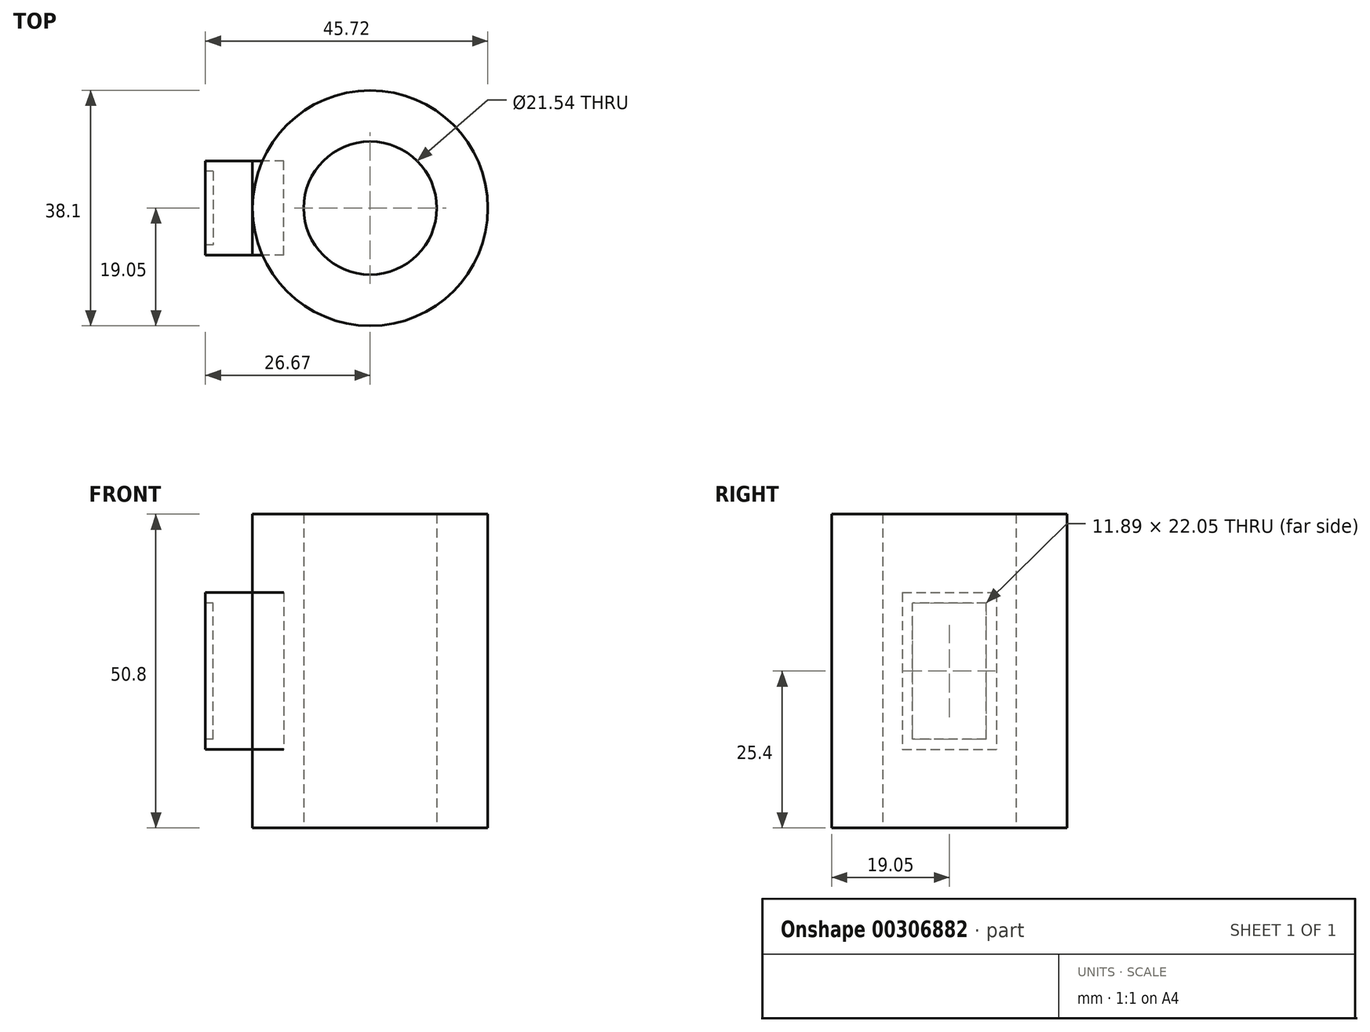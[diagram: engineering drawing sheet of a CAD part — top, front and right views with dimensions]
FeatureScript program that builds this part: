
annotation { "Feature Type Name" : "Feature", "Feature Type Description" : "" }
export const myFeature = defineFeature(function(context is Context, id is Id, definition is map)
    precondition{}
    {
        {
            var Q0;
            Q0=qCreatedBy(makeId("Top.planeOp"),FACE);
            var sketch = newSketch(context, id + "F0", { "sketchPlane" : qUnion([Q0])});
            skCircle(sketch, "E0", {"center": v(0, 0) * mm, "radius": 10.77 * mm});
            skCircle(sketch, "E1", {"center": v(0, 0) * mm, "radius": 19.05 * mm});
            skSolve(sketch);
        }
        {
            var Q0;
            Q0=makeQuery(id+"F0.imprint","IMPRINT",FACE,{"disambiguationData":[TD([[makeQuery(id+"F0.imprint","IMPRINT",EDGE,{"derivedFrom":sQuery(id+"F0.wireOp",EDGE,"E0")}),-1.0]])]});
            extrude(context, id + "F1", {"entities" : qUnion([Q0]), "depth" : 50.8 * mm});
        }
        {
            var Q0;
            Q0=qCreatedBy(makeId("Front.planeOp"),FACE);
            var sketch = newSketch(context, id + "F2", { "sketchPlane" : qUnion([Q0])});
            skLineSegment(sketch, "E2", {"start": v(-19.05, 38.1) * mm, "end": v(-26.67, 38.1) * mm});
            skLineSegment(sketch, "E3", {"start": v(-26.67, 38.1) * mm, "end": v(-26.67, 12.7) * mm});
            skLineSegment(sketch, "E4", {"start": v(-26.67, 12.7) * mm, "end": v(-19.05, 12.7) * mm});
            skLineSegment(sketch, "E5", {"start": v(-19.05, 50.8) * mm, "end": v(-19.05, 0) * mm, "construction": true});
            skLineSegment(sketch, "E6", {"start": v(0, 0) * mm, "end": v(-19.05, 0) * mm, "construction": true});
            skLineSegment(sketch, "E7", {"start": v(-26.67, 25.4) * mm, "end": v(-19.05, 25.4) * mm, "construction": true});
            skLineSegment(sketch, "E8", {"start": v(-19.05, 38.1) * mm, "end": v(-19.05, 12.7) * mm});
            skSolve(sketch);
        }
        {
            var Q0;
            Q0=makeQuery(id+"F2.imprint","IMPRINT",FACE,{"disambiguationData":[TD([[makeQuery(id+"F2.imprint","IMPRINT",EDGE,{"derivedFrom":sQuery(id+"F2.wireOp",EDGE,"E2")}),1.0]])]});
            extrude(context, id + "F3", {"entities" : qUnion([Q0]), "depth" : 7.62 * mm});
        }
        {
            var Q0;
            Q0=makeQuery(id+"F3.opExtrude","CAP_FACE",FACE,{"disambiguationData":[OSD([sQuery(id+"F2.wireOp",EDGE,"E2"),sQuery(id+"F2.wireOp",EDGE,"E3"),sQuery(id+"F2.wireOp",EDGE,"E4"),sQuery(id+"F2.wireOp",EDGE,"E8")])],"isStart":true});
            extrude(context, id + "F4", {"entities" : qUnion([Q0]), "operationType" : NewBodyOperationType.ADD, "depth" : 7.62 * mm});
        }
        {
            var Q0;
            {var subQ0=sQuery(id+"F2.wireOp",EDGE,"E3");Q0=makeQuery(id+"F4.boolean.opBoolean","MERGE",FACE,{"derivedFrom":[makeQuery(id+"F3.opExtrude","SWEPT_FACE",FACE,{"disambiguationData":[OSD([subQ0])]}),makeQuery(id+"F4.opExtrude","SWEPT_FACE",FACE,{"disambiguationData":[OSD([subQ0])]})]});}
            var sketch = newSketch(context, id + "F5", { "sketchPlane" : qUnion([Q0])});
            skLineSegment(sketch, "E9.bottom", {"start": v(-7.62, 12.7) * mm, "end": v(7.62, 12.7) * mm});
            skLineSegment(sketch, "E9.top", {"start": v(-7.62, 38.1) * mm, "end": v(7.62, 38.1) * mm});
            skLineSegment(sketch, "E9.left", {"start": v(-7.62, 12.7) * mm, "end": v(-7.62, 38.1) * mm});
            skLineSegment(sketch, "E9.right", {"start": v(7.62, 12.7) * mm, "end": v(7.62, 38.1) * mm});
            skSolve(sketch);
        }
        {
            var Q0;
            Q0=makeQuery(id+"F5.imprint","IMPRINT",FACE,{"disambiguationData":[TD([[makeQuery(id+"F5.imprint","IMPRINT",EDGE,{"derivedFrom":sQuery(id+"F5.wireOp",EDGE,"E9.bottom")}),-1.0]])]});
            extrude(context, id + "F6", {"entities" : qUnion([Q0]), "oppositeDirection" : true, "depth" : 12.7 * mm});
        }
        {
            var Q0;
            {var subQ0=sQuery(id+"F2.wireOp",EDGE,"E3");Q0=makeQuery(id+"F4.boolean.opBoolean","MERGE",FACE,{"derivedFrom":[makeQuery(id+"F3.opExtrude","SWEPT_FACE",FACE,{"disambiguationData":[OSD([subQ0])]}),makeQuery(id+"F4.opExtrude","SWEPT_FACE",FACE,{"disambiguationData":[OSD([subQ0])]})]});}
            var sketch = newSketch(context, id + "F7", { "sketchPlane" : qUnion([Q0])});
            skLineSegment(sketch, "E10.bottom", {"start": v(-5.94, 14.38) * mm, "end": v(5.94, 14.38) * mm});
            skLineSegment(sketch, "E10.top", {"start": v(-5.94, 36.42) * mm, "end": v(5.94, 36.42) * mm});
            skLineSegment(sketch, "E10.left", {"start": v(-5.94, 14.38) * mm, "end": v(-5.94, 36.42) * mm});
            skLineSegment(sketch, "E10.right", {"start": v(5.94, 14.38) * mm, "end": v(5.94, 36.42) * mm});
            skSolve(sketch);
        }
        {
            var Q0;
            Q0=makeQuery(id+"F7.imprint","IMPRINT",FACE,{"disambiguationData":[TD([[makeQuery(id+"F7.imprint","IMPRINT",EDGE,{"derivedFrom":sQuery(id+"F7.wireOp",EDGE,"E10.bottom")}),1.0]])]});
            extrude(context, id + "F8", {"entities" : qUnion([Q0]), "operationType" : NewBodyOperationType.REMOVE, "oppositeDirection" : true, "depth" : 1.27 * mm});
        }
    });
